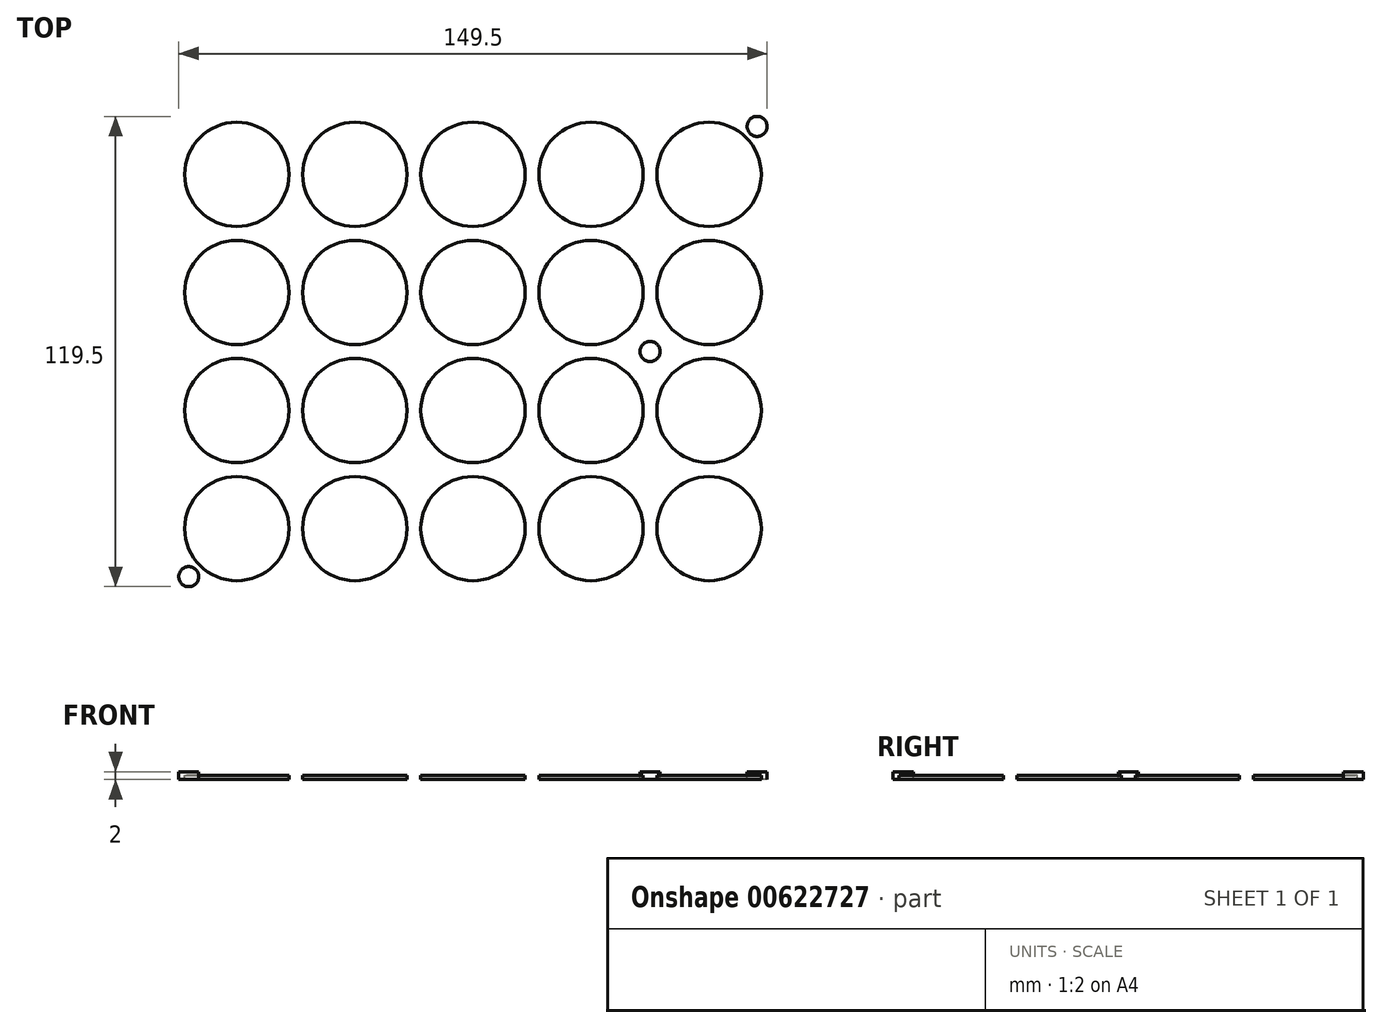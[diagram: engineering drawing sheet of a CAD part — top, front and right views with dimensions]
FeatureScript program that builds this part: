
annotation { "Feature Type Name" : "Feature", "Feature Type Description" : "" }
export const myFeature = defineFeature(function(context is Context, id is Id, definition is map)
    precondition{}
    {
        {
            var Q0;
            Q0=qCreatedBy(makeId("Top.planeOp"),FACE);
            var sketch = newSketch(context, id + "F0", { "sketchPlane" : qUnion([Q0])});
            skLineSegment(sketch, "E0.bottom", {"start": v(-76.25, 61.25) * mm, "end": v(76.25, 61.25) * mm});
            skLineSegment(sketch, "E0.top", {"start": v(-76.25, -61.25) * mm, "end": v(76.25, -61.25) * mm});
            skLineSegment(sketch, "E0.left", {"start": v(-76.25, 61.25) * mm, "end": v(-76.25, -61.25) * mm});
            skLineSegment(sketch, "E0.right", {"start": v(76.25, 61.25) * mm, "end": v(76.25, -61.25) * mm});
            skPoint(sketch, "E0.middle", {"position": v(0, 0) * mm});
            skCircle(sketch, "E1", {"center": v(-60, 45) * mm, "radius": 13.25 * mm});
            skCircle(sketch, "E2.0.1.0", {"center": v(-60, 15) * mm, "radius": 13.25 * mm});
            skCircle(sketch, "E2.0.2.0", {"center": v(-60, -15) * mm, "radius": 13.25 * mm});
            skCircle(sketch, "E2.0.3.0", {"center": v(-60, -45) * mm, "radius": 13.25 * mm});
            skCircle(sketch, "E2.1.0.0", {"center": v(-30, 45) * mm, "radius": 13.25 * mm});
            skCircle(sketch, "E2.1.1.0", {"center": v(-30, 15) * mm, "radius": 13.25 * mm});
            skCircle(sketch, "E2.1.2.0", {"center": v(-30, -15) * mm, "radius": 13.25 * mm});
            skCircle(sketch, "E2.1.3.0", {"center": v(-30, -45) * mm, "radius": 13.25 * mm});
            skCircle(sketch, "E2.2.0.0", {"center": v(0, 45) * mm, "radius": 13.25 * mm});
            skCircle(sketch, "E2.2.1.0", {"center": v(0, 15) * mm, "radius": 13.25 * mm});
            skCircle(sketch, "E2.2.2.0", {"center": v(0, -15) * mm, "radius": 13.25 * mm});
            skCircle(sketch, "E2.2.3.0", {"center": v(0, -45) * mm, "radius": 13.25 * mm});
            skCircle(sketch, "E2.3.0.0", {"center": v(30, 45) * mm, "radius": 13.25 * mm});
            skCircle(sketch, "E2.3.1.0", {"center": v(30, 15) * mm, "radius": 13.25 * mm});
            skCircle(sketch, "E2.3.2.0", {"center": v(30, -15) * mm, "radius": 13.25 * mm});
            skCircle(sketch, "E2.3.3.0", {"center": v(30, -45) * mm, "radius": 13.25 * mm});
            skCircle(sketch, "E2.4.0.0", {"center": v(60, 45) * mm, "radius": 13.25 * mm});
            skCircle(sketch, "E2.4.1.0", {"center": v(60, 15) * mm, "radius": 13.25 * mm});
            skCircle(sketch, "E2.4.2.0", {"center": v(60, -15) * mm, "radius": 13.25 * mm});
            skCircle(sketch, "E2.4.3.0", {"center": v(60, -45) * mm, "radius": 13.25 * mm});
            skLineSegment(sketch, "E2.direction1", {"start": v(-60, 45) * mm, "end": v(-30, 45) * mm, "construction": true});
            skLineSegment(sketch, "E2.direction2", {"start": v(-60, 45) * mm, "end": v(-60, 15) * mm, "construction": true});
            skSolve(sketch);
        }
        {
            var Q0;
            Q0=makeQuery(id+"F0.imprint","IMPRINT",FACE,{"disambiguationData":[TD([[makeQuery(id+"F0.imprint","IMPRINT",EDGE,{"derivedFrom":sQuery(id+"F0.wireOp",EDGE,"E1")}),1.0]])]});
            var Q1;
            Q1=makeQuery(id+"F0.imprint","IMPRINT",FACE,{"disambiguationData":[TD([[makeQuery(id+"F0.imprint","IMPRINT",EDGE,{"derivedFrom":sQuery(id+"F0.wireOp",EDGE,"E2.1.0.0")}),1.0]])]});
            var Q2;
            Q2=makeQuery(id+"F0.imprint","IMPRINT",FACE,{"disambiguationData":[TD([[makeQuery(id+"F0.imprint","IMPRINT",EDGE,{"derivedFrom":sQuery(id+"F0.wireOp",EDGE,"E2.2.0.0")}),1.0]])]});
            var Q3;
            Q3=makeQuery(id+"F0.imprint","IMPRINT",FACE,{"disambiguationData":[TD([[makeQuery(id+"F0.imprint","IMPRINT",EDGE,{"derivedFrom":sQuery(id+"F0.wireOp",EDGE,"E2.3.0.0")}),1.0]])]});
            var Q4;
            Q4=makeQuery(id+"F0.imprint","IMPRINT",FACE,{"disambiguationData":[TD([[makeQuery(id+"F0.imprint","IMPRINT",EDGE,{"derivedFrom":sQuery(id+"F0.wireOp",EDGE,"E2.4.0.0")}),1.0]])]});
            var Q5;
            Q5=makeQuery(id+"F0.imprint","IMPRINT",FACE,{"disambiguationData":[TD([[makeQuery(id+"F0.imprint","IMPRINT",EDGE,{"derivedFrom":sQuery(id+"F0.wireOp",EDGE,"E2.4.1.0")}),1.0]])]});
            var Q6;
            Q6=makeQuery(id+"F0.imprint","IMPRINT",FACE,{"disambiguationData":[TD([[makeQuery(id+"F0.imprint","IMPRINT",EDGE,{"derivedFrom":sQuery(id+"F0.wireOp",EDGE,"E2.3.1.0")}),1.0]])]});
            var Q7;
            Q7=makeQuery(id+"F0.imprint","IMPRINT",FACE,{"disambiguationData":[TD([[makeQuery(id+"F0.imprint","IMPRINT",EDGE,{"derivedFrom":sQuery(id+"F0.wireOp",EDGE,"E0.bottom")}),-1.0]])]});
            var Q8;
            Q8=makeQuery(id+"F0.imprint","IMPRINT",FACE,{"disambiguationData":[TD([[makeQuery(id+"F0.imprint","IMPRINT",EDGE,{"derivedFrom":sQuery(id+"F0.wireOp",EDGE,"E2.1.1.0")}),1.0]])]});
            var Q9;
            Q9=makeQuery(id+"F0.imprint","IMPRINT",FACE,{"disambiguationData":[TD([[makeQuery(id+"F0.imprint","IMPRINT",EDGE,{"derivedFrom":sQuery(id+"F0.wireOp",EDGE,"E2.0.1.0")}),1.0]])]});
            var Q10;
            Q10=makeQuery(id+"F0.imprint","IMPRINT",FACE,{"disambiguationData":[TD([[makeQuery(id+"F0.imprint","IMPRINT",EDGE,{"derivedFrom":sQuery(id+"F0.wireOp",EDGE,"E2.2.1.0")}),1.0]])]});
            var Q11;
            Q11=makeQuery(id+"F0.imprint","IMPRINT",FACE,{"disambiguationData":[TD([[makeQuery(id+"F0.imprint","IMPRINT",EDGE,{"derivedFrom":sQuery(id+"F0.wireOp",EDGE,"E2.2.2.0")}),1.0]])]});
            var Q12;
            Q12=makeQuery(id+"F0.imprint","IMPRINT",FACE,{"disambiguationData":[TD([[makeQuery(id+"F0.imprint","IMPRINT",EDGE,{"derivedFrom":sQuery(id+"F0.wireOp",EDGE,"E2.1.2.0")}),1.0]])]});
            var Q13;
            Q13=makeQuery(id+"F0.imprint","IMPRINT",FACE,{"disambiguationData":[TD([[makeQuery(id+"F0.imprint","IMPRINT",EDGE,{"derivedFrom":sQuery(id+"F0.wireOp",EDGE,"E2.0.2.0")}),1.0]])]});
            var Q14;
            Q14=makeQuery(id+"F0.imprint","IMPRINT",FACE,{"disambiguationData":[TD([[makeQuery(id+"F0.imprint","IMPRINT",EDGE,{"derivedFrom":sQuery(id+"F0.wireOp",EDGE,"E2.3.2.0")}),1.0]])]});
            var Q15;
            Q15=makeQuery(id+"F0.imprint","IMPRINT",FACE,{"disambiguationData":[TD([[makeQuery(id+"F0.imprint","IMPRINT",EDGE,{"derivedFrom":sQuery(id+"F0.wireOp",EDGE,"E2.4.2.0")}),1.0]])]});
            var Q16;
            Q16=makeQuery(id+"F0.imprint","IMPRINT",FACE,{"disambiguationData":[TD([[makeQuery(id+"F0.imprint","IMPRINT",EDGE,{"derivedFrom":sQuery(id+"F0.wireOp",EDGE,"E2.3.3.0")}),1.0]])]});
            var Q17;
            Q17=makeQuery(id+"F0.imprint","IMPRINT",FACE,{"disambiguationData":[TD([[makeQuery(id+"F0.imprint","IMPRINT",EDGE,{"derivedFrom":sQuery(id+"F0.wireOp",EDGE,"E2.4.3.0")}),1.0]])]});
            var Q18;
            Q18=makeQuery(id+"F0.imprint","IMPRINT",FACE,{"disambiguationData":[TD([[makeQuery(id+"F0.imprint","IMPRINT",EDGE,{"derivedFrom":sQuery(id+"F0.wireOp",EDGE,"E2.4.4.0")}),1.0]])]});
            var Q19;
            Q19=makeQuery(id+"F0.imprint","IMPRINT",FACE,{"disambiguationData":[TD([[makeQuery(id+"F0.imprint","IMPRINT",EDGE,{"derivedFrom":sQuery(id+"F0.wireOp",EDGE,"E2.3.4.0")}),1.0]])]});
            var Q20;
            Q20=makeQuery(id+"F0.imprint","IMPRINT",FACE,{"disambiguationData":[TD([[makeQuery(id+"F0.imprint","IMPRINT",EDGE,{"derivedFrom":sQuery(id+"F0.wireOp",EDGE,"E2.2.4.0")}),1.0]])]});
            var Q21;
            Q21=makeQuery(id+"F0.imprint","IMPRINT",FACE,{"disambiguationData":[TD([[makeQuery(id+"F0.imprint","IMPRINT",EDGE,{"derivedFrom":sQuery(id+"F0.wireOp",EDGE,"E2.2.3.0")}),1.0]])]});
            var Q22;
            Q22=makeQuery(id+"F0.imprint","IMPRINT",FACE,{"disambiguationData":[TD([[makeQuery(id+"F0.imprint","IMPRINT",EDGE,{"derivedFrom":sQuery(id+"F0.wireOp",EDGE,"E2.1.4.0")}),1.0]])]});
            var Q23;
            Q23=makeQuery(id+"F0.imprint","IMPRINT",FACE,{"disambiguationData":[TD([[makeQuery(id+"F0.imprint","IMPRINT",EDGE,{"derivedFrom":sQuery(id+"F0.wireOp",EDGE,"E2.1.3.0")}),1.0]])]});
            var Q24;
            Q24=makeQuery(id+"F0.imprint","IMPRINT",FACE,{"disambiguationData":[TD([[makeQuery(id+"F0.imprint","IMPRINT",EDGE,{"derivedFrom":sQuery(id+"F0.wireOp",EDGE,"E2.0.3.0")}),1.0]])]});
            var Q25;
            Q25=makeQuery(id+"F0.imprint","IMPRINT",FACE,{"disambiguationData":[TD([[makeQuery(id+"F0.imprint","IMPRINT",EDGE,{"derivedFrom":sQuery(id+"F0.wireOp",EDGE,"E2.0.4.0")}),1.0]])]});
            extrude(context, id + "F1", {"entities" : qUnion([Q0, Q1, Q2, Q3, Q4, Q5, Q6, Q7, Q8, Q9, Q10, Q11, Q12, Q13, Q14, Q15, Q16, Q17, Q18, Q19, Q20, Q21, Q22, Q23, Q24, Q25]), "depth" : 1 * mm, "offsetDistance" : 25 * mm});
        }
        {
            var Q0;
            Q0=qSketchRegion(id+"F0",true);
            extrude(context, id + "F2", {"entities" : qUnion([Q0]), "operationType" : NewBodyOperationType.ADD, "depth" : 2 * mm, "offsetDistance" : 25 * mm});
        }
        {
            var Q0;
            Q0=makeQuery(id+"F2.opExtrude","CAP_FACE",FACE,{"disambiguationData":[OSD([sQuery(id+"F0.wireOp",EDGE,"E0.bottom"),sQuery(id+"F0.wireOp",EDGE,"E0.top"),sQuery(id+"F0.wireOp",EDGE,"E0.left"),sQuery(id+"F0.wireOp",EDGE,"E0.right"),sQuery(id+"F0.wireOp",EDGE,"E1"),sQuery(id+"F0.wireOp",EDGE,"E2.0.1.0"),sQuery(id+"F0.wireOp",EDGE,"E2.0.2.0"),sQuery(id+"F0.wireOp",EDGE,"E2.0.3.0"),sQuery(id+"F0.wireOp",EDGE,"E2.0.4.0"),sQuery(id+"F0.wireOp",EDGE,"E2.1.0.0"),sQuery(id+"F0.wireOp",EDGE,"E2.1.1.0"),sQuery(id+"F0.wireOp",EDGE,"E2.1.2.0"),sQuery(id+"F0.wireOp",EDGE,"E2.1.3.0"),sQuery(id+"F0.wireOp",EDGE,"E2.1.4.0"),sQuery(id+"F0.wireOp",EDGE,"E2.2.0.0"),sQuery(id+"F0.wireOp",EDGE,"E2.2.1.0"),sQuery(id+"F0.wireOp",EDGE,"E2.2.2.0"),sQuery(id+"F0.wireOp",EDGE,"E2.2.3.0"),sQuery(id+"F0.wireOp",EDGE,"E2.2.4.0"),sQuery(id+"F0.wireOp",EDGE,"E2.3.0.0"),sQuery(id+"F0.wireOp",EDGE,"E2.3.1.0"),sQuery(id+"F0.wireOp",EDGE,"E2.3.2.0"),sQuery(id+"F0.wireOp",EDGE,"E2.3.3.0"),sQuery(id+"F0.wireOp",EDGE,"E2.3.4.0"),sQuery(id+"F0.wireOp",EDGE,"E2.4.0.0"),sQuery(id+"F0.wireOp",EDGE,"E2.4.1.0"),sQuery(id+"F0.wireOp",EDGE,"E2.4.2.0"),sQuery(id+"F0.wireOp",EDGE,"E2.4.3.0"),sQuery(id+"F0.wireOp",EDGE,"E2.4.4.0")])],"isStart":false});
            var sketch = newSketch(context, id + "F3", { "sketchPlane" : qUnion([Q0])});
            skLineSegment(sketch, "E3", {"start": v(0, 74.2) * mm, "end": v(0, -73.43) * mm, "construction": true});
            skLineSegment(sketch, "E4", {"start": v(-81.9, 0) * mm, "end": v(78.5, 0) * mm, "construction": true});
            skCircle(sketch, "E5", {"center": v(-72.2, 57.2) * mm, "radius": 2.55 * mm});
            skCircle(sketch, "E6", {"center": v(-45, 0) * mm, "radius": 2.55 * mm});
            skCircle(sketch, "E7.MirrorC", {"center": v(72.2, 57.2) * mm, "radius": 2.55 * mm});
            skCircle(sketch, "E8.MirrorC", {"center": v(45, 0) * mm, "radius": 2.55 * mm});
            skCircle(sketch, "E9.MirrorC", {"center": v(72.2, -57.2) * mm, "radius": 2.55 * mm});
            skCircle(sketch, "E10.MirrorC", {"center": v(-72.2, -57.2) * mm, "radius": 2.55 * mm});
            skSolve(sketch);
        }
        {
            var Q0;
            Q0=makeQuery(id+"F3.imprint","IMPRINT",FACE,{"disambiguationData":[TD([[makeQuery(id+"F3.imprint","IMPRINT",EDGE,{"derivedFrom":sQuery(id+"F3.wireOp",EDGE,"E5")}),1.0]])]});
            var Q1;
            Q1=makeQuery(id+"F3.imprint","IMPRINT",FACE,{"disambiguationData":[TD([[makeQuery(id+"F3.imprint","IMPRINT",EDGE,{"derivedFrom":sQuery(id+"F3.wireOp",EDGE,"E7.MirrorC")}),-1.0]])]});
            var Q2;
            Q2=makeQuery(id+"F3.imprint","IMPRINT",FACE,{"disambiguationData":[TD([[makeQuery(id+"F3.imprint","IMPRINT",EDGE,{"derivedFrom":sQuery(id+"F3.wireOp",EDGE,"E8.MirrorC")}),-1.0]])]});
            var Q3;
            Q3=makeQuery(id+"F3.imprint","IMPRINT",FACE,{"disambiguationData":[TD([[makeQuery(id+"F3.imprint","IMPRINT",EDGE,{"derivedFrom":sQuery(id+"F3.wireOp",EDGE,"E6")}),1.0]])]});
            var Q4;
            Q4=makeQuery(id+"F3.imprint","IMPRINT",FACE,{"disambiguationData":[TD([[makeQuery(id+"F3.imprint","IMPRINT",EDGE,{"derivedFrom":sQuery(id+"F3.wireOp",EDGE,"E8.MirrorC")}),1.0]])]});
            var Q5;
            Q5=makeQuery(id+"F3.imprint","IMPRINT",FACE,{"disambiguationData":[TD([[makeQuery(id+"F3.imprint","IMPRINT",EDGE,{"derivedFrom":sQuery(id+"F3.wireOp",EDGE,"E6")}),-1.0]])]});
            var Q6;
            Q6=makeQuery(id+"F3.imprint","IMPRINT",FACE,{"disambiguationData":[TD([[makeQuery(id+"F3.imprint","IMPRINT",EDGE,{"derivedFrom":sQuery(id+"F3.wireOp",EDGE,"E10.MirrorC")}),-1.0]])]});
            var Q7;
            Q7=makeQuery(id+"F3.imprint","IMPRINT",FACE,{"disambiguationData":[TD([[makeQuery(id+"F3.imprint","IMPRINT",EDGE,{"derivedFrom":sQuery(id+"F3.wireOp",EDGE,"E9.MirrorC")}),1.0]])]});
            extrude(context, id + "F4", {"entities" : qUnion([Q0, Q1, Q2, Q3, Q4, Q5, Q6, Q7]), "operationType" : NewBodyOperationType.REMOVE, "endBound" : BoundingType.THROUGH_ALL, "oppositeDirection" : true, "depth" : 25 * mm, "offsetDistance" : 25 * mm});
        }
    });
